# Revit family: 601-A-009-DN65-200
name_source: partatom
category: Pipe Accessories
units: mm (PartAtom-declared; Revit-internal decimal feet)

## family parameters
Always vertical = Yes
Cut with Voids When Loaded = No
Part Type = Valve - Breaks Into
Round Connector Dimension = Use Diameter
Shared = No
Work Plane-Based = No

## types (9) — shared parameters
DN065_68-85 = 601-085-000-6100
DN080_99-119 = 601-119-000-6100
DN100_109-133 = 601-133-000-6100
DN125_132-157 = 601-157-000-6100
DN150_157-183 = 601-183-000-6100
DN150_176-201 = 601-201-000-6100
DN175_193-215 = 601-215-000-6100
DN200_218-242 = 601-242-000-6100
Description_ = AVK UNIVERSAL SUPA® STRAIGHT COUPLING
F = 5 mm  [stored 0.0164042 ft]
Search_Table = 601-A-009-DN65-200
URL_product_pages = https://www.avkvalves.com
W1 = 32 mm  [stored 0.104987 ft]

## per-type parameters (varying)
| type | B2 | Body_height | Body_height_ref | D | D2 | D3 | DN | DN080_84-106 | DN2 | DN_ref | ID | L | L1 | PCD | W2 |
| DN065_68-85 | 82 mm  [stored 0.269029 ft] | 164 mm | 152 mm | 80 mm  [stored 0.262467 ft] | 52 mm | 220 mm | 65 mm  [stored 0.213255 ft] | 601-074-000-6100 | 85 mm  [stored 0.278871 ft] | 43 mm  [stored 0.141076 ft] | 33 mm | 197 mm | 100 mm  [stored 0.328084 ft] | 185 mm | 105 mm  [stored 0.344488 ft] |
| DN080_84-106 | 83 mm  [stored 0.27231 ft] | 166 mm | 154 mm | 77 mm  [stored 0.252625 ft] | 60 mm  [stored 0.19685 ft] | 226 mm | 80 mm  [stored 0.262467 ft] | 601-074-000-6100 | 106 mm  [stored 0.347769 ft] | 53 mm  [stored 0.173885 ft] | 40 mm  [stored 0.131234 ft] | 197 mm | 100 mm  [stored 0.328084 ft] | 190 mm | 108 mm  [stored 0.354331 ft] |
| DN080_99-119 | 83 mm  [stored 0.27231 ft] | 166 mm | 154 mm | 77 mm  [stored 0.252625 ft] | 67 mm  [stored 0.219816 ft] | 226 mm | 80 mm  [stored 0.262467 ft] | 601-074-000-6100 | 119 mm  [stored 0.39042 ft] | 60 mm  [stored 0.19685 ft] | 40 mm  [stored 0.131234 ft] | 197 mm | 100 mm  [stored 0.328084 ft] | 190 mm | 108 mm  [stored 0.354331 ft] |
| DN100_109-133 | 85 mm  [stored 0.278871 ft] | 169 mm | 157 mm | 93 mm  [stored 0.305118 ft] | 78 mm | 244 mm | 100 mm  [stored 0.328084 ft] | 601-074-000-6100 | 133 mm  [stored 0.436352 ft] | 67 mm  [stored 0.219816 ft] | 50 mm  [stored 0.164042 ft] | 197 mm | 100 mm  [stored 0.328084 ft] | 208 mm | 117 mm  [stored 0.383858 ft] |
| DN125_132-157 | 85 mm  [stored 0.278871 ft] | 169 mm | 157 mm | 106 mm  [stored 0.347769 ft] | 88 mm  [stored 0.288714 ft] | 270 mm | 125 mm  [stored 0.410105 ft] | 601-106-000-6100 | 157 mm | 79 mm | 63 mm  [stored 0.206693 ft] | 197 mm | 100 mm  [stored 0.328084 ft] | 235 mm | 130 mm  [stored 0.426509 ft] |
| DN150_157-183 | 93 mm  [stored 0.305118 ft] | 185 mm | 173 mm | 120 mm  [stored 0.393701 ft] | 100 mm  [stored 0.328084 ft] | 300 mm | 150 mm  [stored 0.492126 ft] | 601-106-000-6100 | 183 mm | 92 mm  [stored 0.301837 ft] | 75 mm | 217 mm | 115 mm  [stored 0.377297 ft] | 264 mm | 145 mm |
| DN150_176-201 | 93 mm  [stored 0.305118 ft] | 185 mm | 173 mm | 120 mm  [stored 0.393701 ft] | 108 mm  [stored 0.354331 ft] | 300 mm | 150 mm  [stored 0.492126 ft] | 601-106-000-6100 | 201 mm | 101 mm | 75 mm | 217 mm | 115 mm  [stored 0.377297 ft] | 264 mm | 145 mm |
| DN175_193-215 | 92 mm  [stored 0.301837 ft] | 183 mm | 171 mm | 134 mm | 115 mm  [stored 0.377297 ft] | 327 mm | 175 mm | 601-106-000-6100 | 215 mm | 108 mm  [stored 0.354331 ft] | 88 mm  [stored 0.288714 ft] | 217 mm | 115 mm  [stored 0.377297 ft] | 281 mm | 159 mm |
| DN200_218-242 | 105 mm  [stored 0.344488 ft] | 209 mm | 197 mm | 150 mm  [stored 0.492126 ft] | 130 mm  [stored 0.426509 ft] | 357 mm | 200 mm | 601-106-000-6100 | 242 mm | 121 mm  [stored 0.396982 ft] | 100 mm  [stored 0.328084 ft] | 237 mm | 140 mm  [stored 0.459318 ft] | 291 mm | 174 mm |

note: [stored X ft] marks values corroborated as IEEE doubles in the binary element streams (Revit-internal decimal feet)

## geometry (parser evidence)
native form markers: Sweep x8
no freeform markers — native parametric forms only
